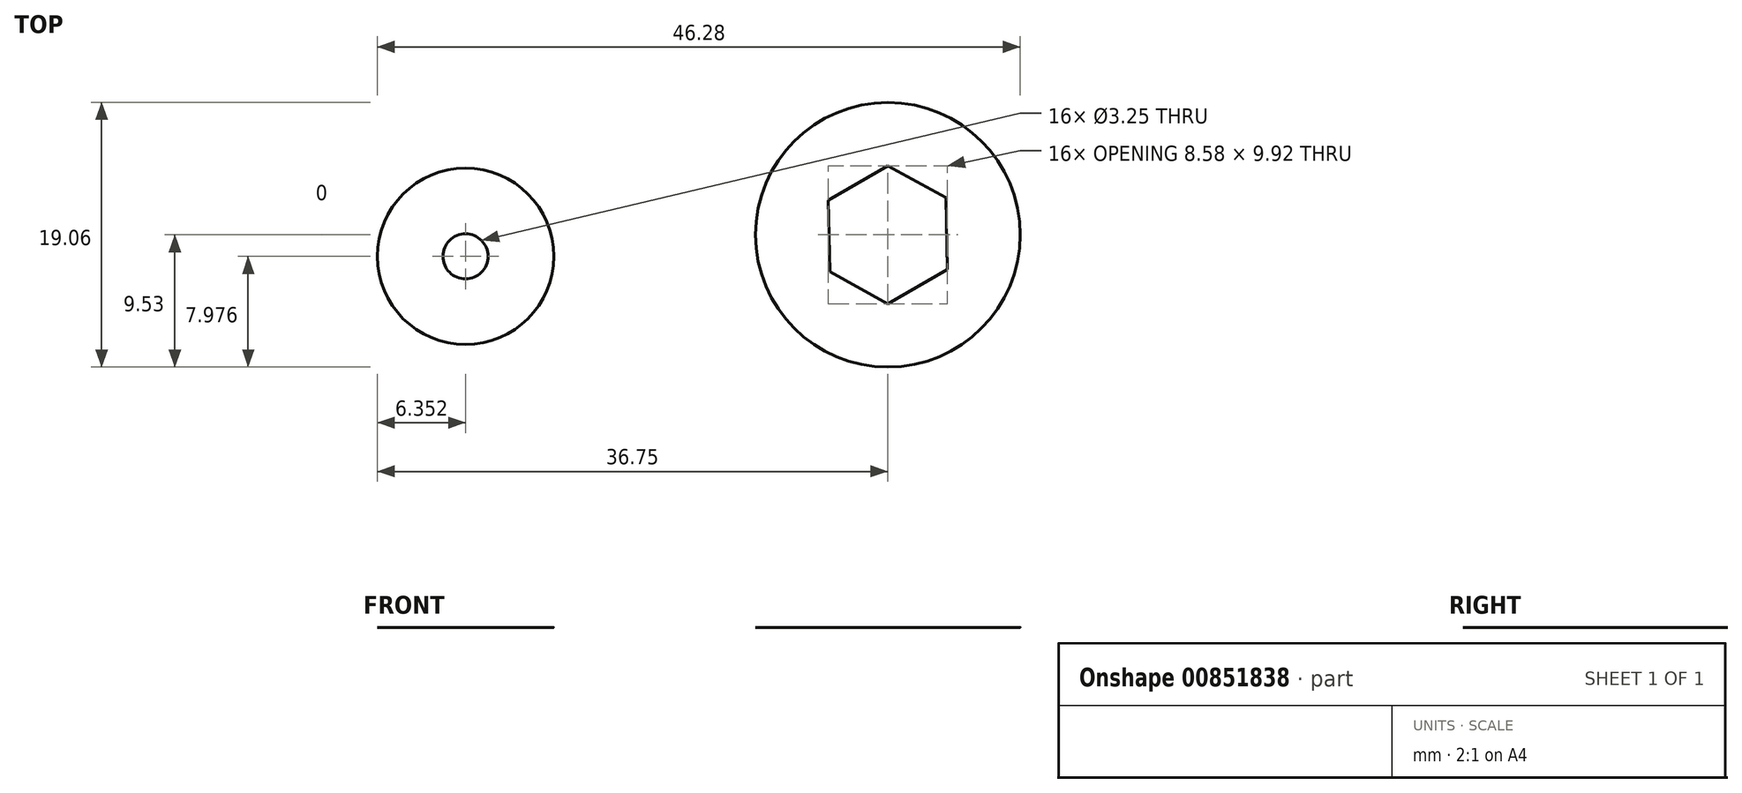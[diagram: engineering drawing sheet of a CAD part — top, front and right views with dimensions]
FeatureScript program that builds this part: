
annotation { "Feature Type Name" : "Feature", "Feature Type Description" : "" }
export const myFeature = defineFeature(function(context is Context, id is Id, definition is map)
    precondition{}
    {
        {
            var Q0;
            Q0=qCreatedBy(makeId("Top.planeOp"),FACE);
            var sketch = newSketch(context, id + "F0", { "sketchPlane" : qUnion([Q0])});
            skLineSegment(sketch, "E0", {"start": v(0, 4.96) * mm, "end": v(0, 0) * mm, "construction": true});
            skLineSegment(sketch, "E1", {"start": v(0, 0) * mm, "end": v(4.29, -2.5) * mm, "construction": true});
            skLineSegment(sketch, "E2", {"start": v(0, 0) * mm, "end": v(-4.29, 2.5) * mm, "construction": true});
            skLineSegment(sketch, "E3", {"start": v(0, 0) * mm, "end": v(0, -4.96) * mm, "construction": true});
            skLineSegment(sketch, "E4", {"start": v(-4.18, -2.67) * mm, "end": v(4.18, 2.67) * mm, "construction": true});
            skLineSegment(sketch, "E5", {"start": v(-4.29, 2.5) * mm, "end": v(0, 4.96) * mm});
            skLineSegment(sketch, "E6", {"start": v(0, 4.96) * mm, "end": v(4.18, 2.67) * mm});
            skLineSegment(sketch, "E7", {"start": v(4.29, -2.5) * mm, "end": v(4.18, 2.67) * mm});
            skLineSegment(sketch, "E8", {"start": v(4.29, -2.5) * mm, "end": v(0, -4.96) * mm});
            skLineSegment(sketch, "E9", {"start": v(-4.18, -2.67) * mm, "end": v(0, -4.96) * mm});
            skLineSegment(sketch, "E10", {"start": v(-4.18, -2.67) * mm, "end": v(-4.29, 2.5) * mm});
            skCircle(sketch, "E11", {"center": v(0, 0) * mm, "radius": 9.53 * mm});
            skCircle(sketch, "E12", {"center": v(-30.4, -1.55) * mm, "radius": 6.35 * mm});
            skCircle(sketch, "E13", {"center": v(-30.4, -1.55) * mm, "radius": 1.63 * mm});
            skSolve(sketch);
        }
        {
            var Q0;
            Q0=makeQuery(id+"F0.imprint","IMPRINT",FACE,{"disambiguationData":[TD([[makeQuery(id+"F0.imprint","IMPRINT",EDGE,{"derivedFrom":sQuery(id+"F0.wireOp",EDGE,"E12")}),1.0]])]});
            var Q1;
            Q1=makeQuery(id+"F0.imprint","IMPRINT",FACE,{"disambiguationData":[TD([[makeQuery(id+"F0.imprint","IMPRINT",EDGE,{"derivedFrom":sQuery(id+"F0.wireOp",EDGE,"E5")}),1.0]])]});
            extrude(context, id + "F1", {"entities" : qUnion([Q0, Q1]), "depth" : 1 / 203.2 * mm, "offsetDistance" : 25.4 * mm});
        }
    });
